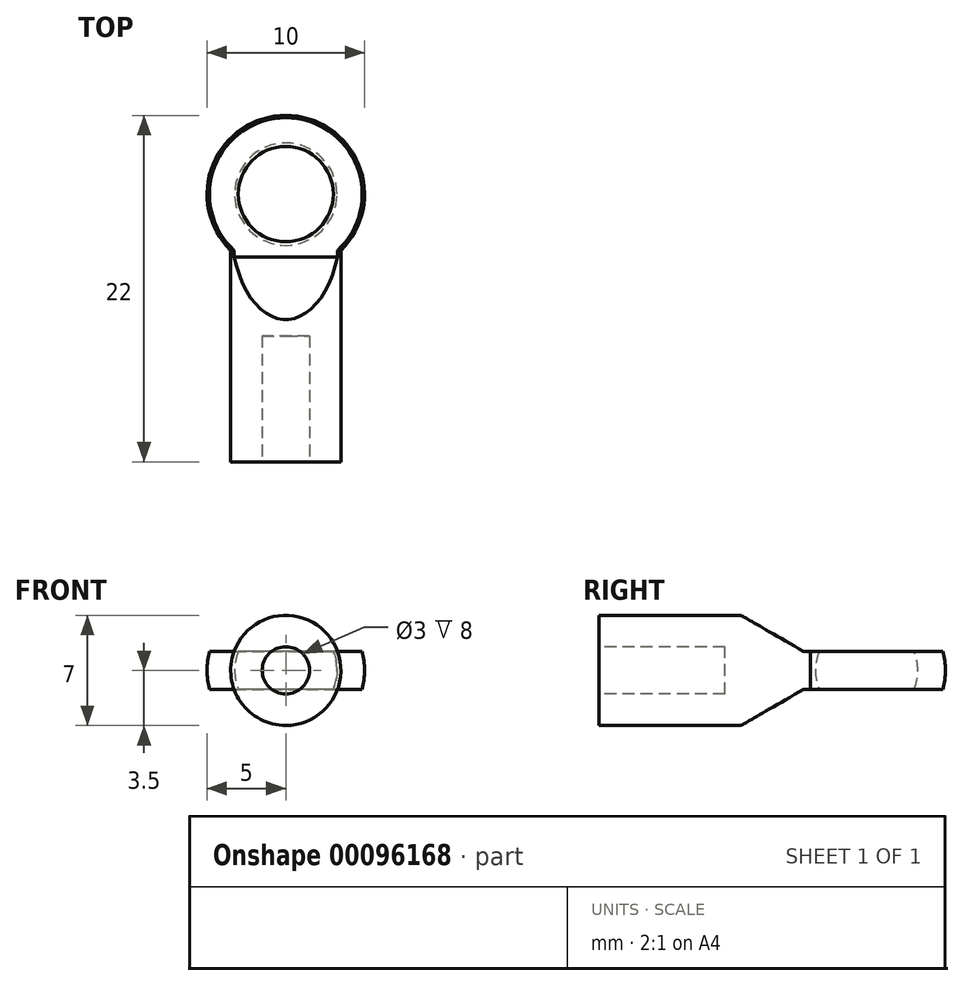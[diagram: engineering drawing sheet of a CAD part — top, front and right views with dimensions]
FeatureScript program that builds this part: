
annotation { "Feature Type Name" : "Feature", "Feature Type Description" : "" }
export const myFeature = defineFeature(function(context is Context, id is Id, definition is map)
    precondition{}
    {
        {
            var Q0;
            Q0=qCreatedBy(makeId("Right.planeOp"),FACE);
            var sketch = newSketch(context, id + "F0", { "sketchPlane" : qUnion([Q0])});
            skArc(sketch, "E0", {"start": v(0, -5) * mm, "mid": v(5, 0) * mm, "end": v(0, 5) * mm});
            skLineSegment(sketch, "E1", {"start": v(0, 5) * mm, "end": v(0, -5) * mm});
            skSolve(sketch);
        }
        {
            var Q0;
            Q0=qSketchRegion(id+"F0",true);
            var Q1;
            Q1=sQuery(id+"F0.wireOp",EDGE,"E1");
            revolve(context, id + "F1", {"entities" : qUnion([Q0]), "axis" : qUnion([Q1]), "revolveType" : RevolveType.FULL});
        }
        {
            var Q0;
            Q0=qCreatedBy(makeId("Front.planeOp"),FACE);
            var sketch = newSketch(context, id + "F2", { "sketchPlane" : qUnion([Q0])});
            skCircle(sketch, "E2", {"center": v(0, 0) * mm, "radius": 3.5 * mm});
            skSolve(sketch);
        }
        {
            var Q0;
            Q0=qSketchRegion(id+"F2",true);
            extrude(context, id + "F3", {"entities" : qUnion([Q0]), "operationType" : NewBodyOperationType.ADD, "depth" : 17 * mm});
        }
        {
            var Q0;
            Q0=qCreatedBy(makeId("Right.planeOp"),FACE);
            var sketch = newSketch(context, id + "F4", { "sketchPlane" : qUnion([Q0])});
            skArc(sketch, "E3", {"start": v(0, -3.25) * mm, "mid": v(3.25, 0) * mm, "end": v(0, 3.25) * mm});
            skLineSegment(sketch, "E4", {"start": v(0, 3.25) * mm, "end": v(0, -3.25) * mm});
            skSolve(sketch);
        }
        {
            var Q0;
            Q0=qSketchRegion(id+"F4",true);
            var Q1;
            Q1=sQuery(id+"F4.wireOp",EDGE,"E4");
            revolve(context, id + "F5", {"operationType" : NewBodyOperationType.REMOVE, "entities" : qUnion([Q0]), "axis" : qUnion([Q1]), "revolveType" : RevolveType.FULL, "oppositeDirection" : true});
        }
        {
            var Q0;
            Q0=qCreatedBy(makeId("Right.planeOp"),FACE);
            var sketch = newSketch(context, id + "F6", { "sketchPlane" : qUnion([Q0])});
            skLineSegment(sketch, "E5", {"start": v(5.5, 1.2) * mm, "end": v(-4, 1.2) * mm});
            skLineSegment(sketch, "E6", {"start": v(-4, 1.2) * mm, "end": v(-10.93, 5.2) * mm});
            skLineSegment(sketch, "E7", {"start": v(-10.93, 5.2) * mm, "end": v(5.5, 5.2) * mm});
            skLineSegment(sketch, "E8", {"start": v(5.5, 5.2) * mm, "end": v(5.5, 1.2) * mm});
            skLineSegment(sketch, "E9.MirrorCS", {"start": v(5.5, -5.2) * mm, "end": v(5.5, -1.2) * mm});
            skLineSegment(sketch, "E10.MirrorCS", {"start": v(-10.93, -5.2) * mm, "end": v(5.5, -5.2) * mm});
            skLineSegment(sketch, "E11.MirrorCS", {"start": v(5.5, -1.2) * mm, "end": v(-4, -1.2) * mm});
            skLineSegment(sketch, "E12.MirrorCS", {"start": v(-4, -1.2) * mm, "end": v(-10.93, -5.2) * mm});
            skSolve(sketch);
        }
        {
            var Q0;
            Q0=qSketchRegion(id+"F6",true);
            extrude(context, id + "F7", {"entities" : qUnion([Q0]), "operationType" : NewBodyOperationType.REMOVE, "oppositeDirection" : true, "depth" : 6 * mm, "hasSecondDirection" : true, "secondDirectionOppositeDirection" : false, "secondDirectionDepth" : 6 * mm});
        }
        {
            var Q0;
            Q0=makeQuery(id+"F3.opExtrude","CAP_FACE",FACE,{"disambiguationData":[OSD([sQuery(id+"F2.wireOp",EDGE,"E2")])],"isStart":false});
            var sketch = newSketch(context, id + "F8", { "sketchPlane" : qUnion([Q0])});
            skCircle(sketch, "E13", {"center": v(0, 0) * mm, "radius": 1.5 * mm});
            skSolve(sketch);
        }
        {
            var Q0;
            Q0=qSketchRegion(id+"F8",true);
            extrude(context, id + "F9", {"entities" : qUnion([Q0]), "operationType" : NewBodyOperationType.REMOVE, "oppositeDirection" : true, "depth" : 8 * mm});
        }
    });
